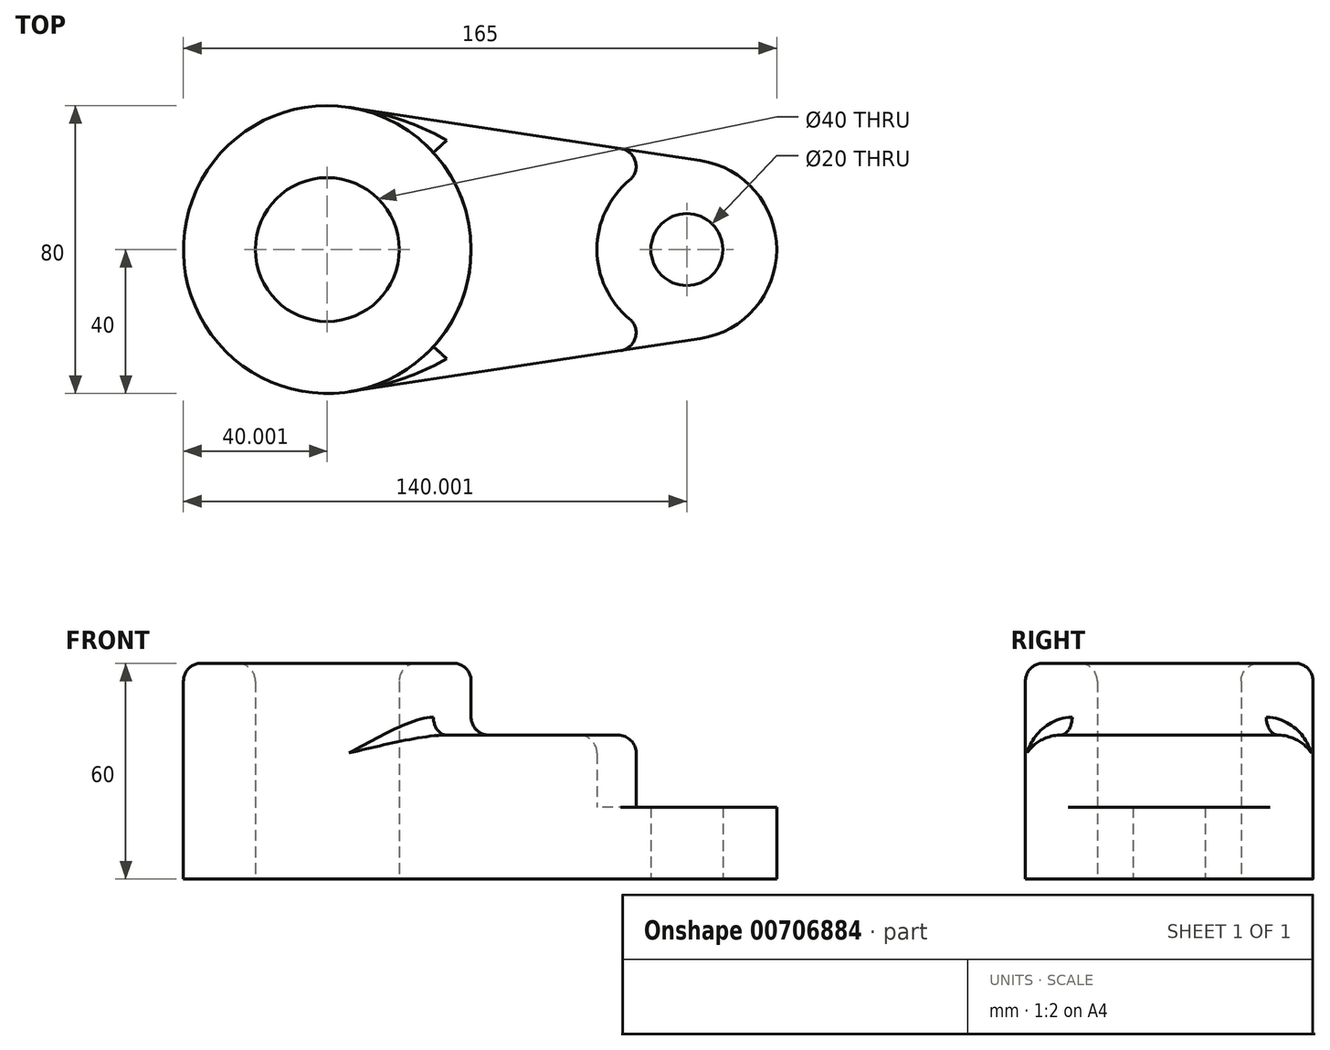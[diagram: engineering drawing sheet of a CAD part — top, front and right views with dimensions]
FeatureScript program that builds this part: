
annotation { "Feature Type Name" : "Feature", "Feature Type Description" : "" }
export const myFeature = defineFeature(function(context is Context, id is Id, definition is map)
    precondition{}
    {
        {
            var Q0;
            Q0=qCreatedBy(makeId("Top.planeOp"),FACE);
            var sketch = newSketch(context, id + "F0", { "sketchPlane" : qUnion([Q0])});
            skCircle(sketch, "E0", {"center": v(-45.99, 0) * mm, "radius": 40 * mm});
            skCircle(sketch, "E1", {"center": v(-45.99, 0) * mm, "radius": 20 * mm});
            skCircle(sketch, "E2", {"center": v(54.01, 0) * mm, "radius": 25 * mm});
            skLineSegment(sketch, "E3", {"start": v(-39.99, 39.55) * mm, "end": v(57.76, 24.72) * mm});
            skLineSegment(sketch, "E4", {"start": v(-39.99, -39.55) * mm, "end": v(57.76, -24.72) * mm});
            skCircle(sketch, "E5", {"center": v(54.01, 0) * mm, "radius": 10 * mm});
            skSolve(sketch);
        }
        {
            var Q0;
            Q0=makeQuery(id+"F0.imprint","IMPRINT",FACE,{"disambiguationData":[TD([[makeQuery(id+"F0.imprint","IMPRINT",EDGE,{"derivedFrom":sQuery(id+"F0.wireOp",EDGE,"E1")}),-1.0]])]});
            extrude(context, id + "F1", {"entities" : qUnion([Q0]), "depth" : 60 * mm, "offsetDistance" : 25 * mm});
        }
        {
            var Q0;
            {var subQ0=sQuery(id+"F0.wireOp",EDGE,"E3");Q0=makeQuery(id+"F0.imprint","IMPRINT",FACE,{"disambiguationData":[TD([[makeQuery(id+"F0.imprint","IMPRINT",EDGE,{"derivedFrom":subQ0}),-1.0]])]});}
            extrude(context, id + "F2", {"entities" : qUnion([Q0]), "operationType" : NewBodyOperationType.ADD, "depth" : 40 * mm, "offsetDistance" : 25 * mm});
        }
        {
            var Q0;
            Q0=makeQuery(id+"F0.imprint","IMPRINT",FACE,{"disambiguationData":[TD([[makeQuery(id+"F0.imprint","IMPRINT",EDGE,{"derivedFrom":sQuery(id+"F0.wireOp",EDGE,"E5")}),-1.0]])]});
            extrude(context, id + "F3", {"entities" : qUnion([Q0]), "operationType" : NewBodyOperationType.ADD, "depth" : 20 * mm, "offsetDistance" : 25 * mm});
        }
        {
            var Q0;
            Q0=makeQuery(id+"F1.opExtrude","CAP_FACE",FACE,{"disambiguationData":[OSD([sQuery(id+"F0.wireOp",EDGE,"E0"),sQuery(id+"F0.wireOp",EDGE,"E1")])],"isStart":false});
            var Q1;
            Q1=makeQuery(id+"F2.opExtrude","CAP_FACE",FACE,{"disambiguationData":[OSD([sQuery(id+"F0.wireOp",EDGE,"E0"),sQuery(id+"F0.wireOp",EDGE,"E2"),sQuery(id+"F0.wireOp",EDGE,"E3"),sQuery(id+"F0.wireOp",EDGE,"E4")])],"isStart":false});
            var Q2;
            {var subQ0=sQuery(id+"F0.wireOp",EDGE,"E2");var subQ1=sQuery(id+"F0.wireOp",EDGE,"E4");Q2=makeQuery(id+"F3.boolean.opBoolean","SPLIT",EDGE,{"disambiguationData":[topologyDisambiguationEdgeConnected([makeQuery(id+"F2.opExtrude","SWEPT_FACE",FACE,{"disambiguationData":[OSD([subQ0])]})])],"derivedFrom":makeQuery(id+"F2.opExtrude","SWEPT_EDGE",EDGE,{"disambiguationData":[OSD([subQ0,subQ1])]})});}
            var Q3;
            {var subQ0=sQuery(id+"F0.wireOp",EDGE,"E2");var subQ1=sQuery(id+"F0.wireOp",EDGE,"E3");Q3=makeQuery(id+"F3.boolean.opBoolean","SPLIT",EDGE,{"disambiguationData":[topologyDisambiguationEdgeConnected([makeQuery(id+"F2.opExtrude","SWEPT_FACE",FACE,{"disambiguationData":[OSD([subQ0])]})])],"derivedFrom":makeQuery(id+"F2.opExtrude","SWEPT_EDGE",EDGE,{"disambiguationData":[OSD([subQ0,subQ1])]})});}
            fillet(context, id + "F4", {"entities" : qUnion([Q0, Q1, Q2, Q3]), "radius" : 5 * mm, "tangentPropagation" : true, "allowEdgeOverflow" : false});
        }
    });
